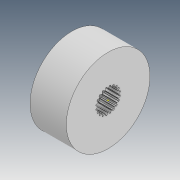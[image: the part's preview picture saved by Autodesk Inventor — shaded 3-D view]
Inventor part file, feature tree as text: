
AUTODESK INVENTOR PART (.ipt)
format: ipt  version: 2021 (Build 250183000, 183)  size: 302,080 bytes
history: native  units: in
note: dims shown in document units (in); Inventor stores cm internally (conversion verified against a paired STEP export)
features: sketch x5, extrude x3, other x2
ambient origin geometry x8: Origin, YZ Plane, XZ Plane, XY Plane, X Axis, Y Axis, Z Axis, Center Point
bodies: Body1 (feature_tree)
feature tree (10):
  other  "Sólido1"
  other  "Revolução1"
  sketch  "Esboço12"  dims[d2=90.0deg d71=0.3346in]
  extrude  "Extrusão6"  Depth=0.3858in
  extrude  "Extrusão7"  Depth=0.3346in
  extrude  "Extrusão8"  Depth=0.1378in
  sketch  "Esboço2"  dims[d0=0.374in d1=0.3858in]
  sketch  "Esboço13"  dims[d72=0.3543in d73=0.1378in]
  sketch  "Esboço14"  dims[d74=0.1516in d75=0.0in]
  sketch  "Esboço15"  dims[d76=0.3543in d77=0.0394in d78=0.0in d79=0.1969in d80=0.2283in d81=0.002in d82=0.002in d83=0.0184in d85=0.002in d86=7.874in d88=360.0deg d90=0.1378in d91=0.0in]
